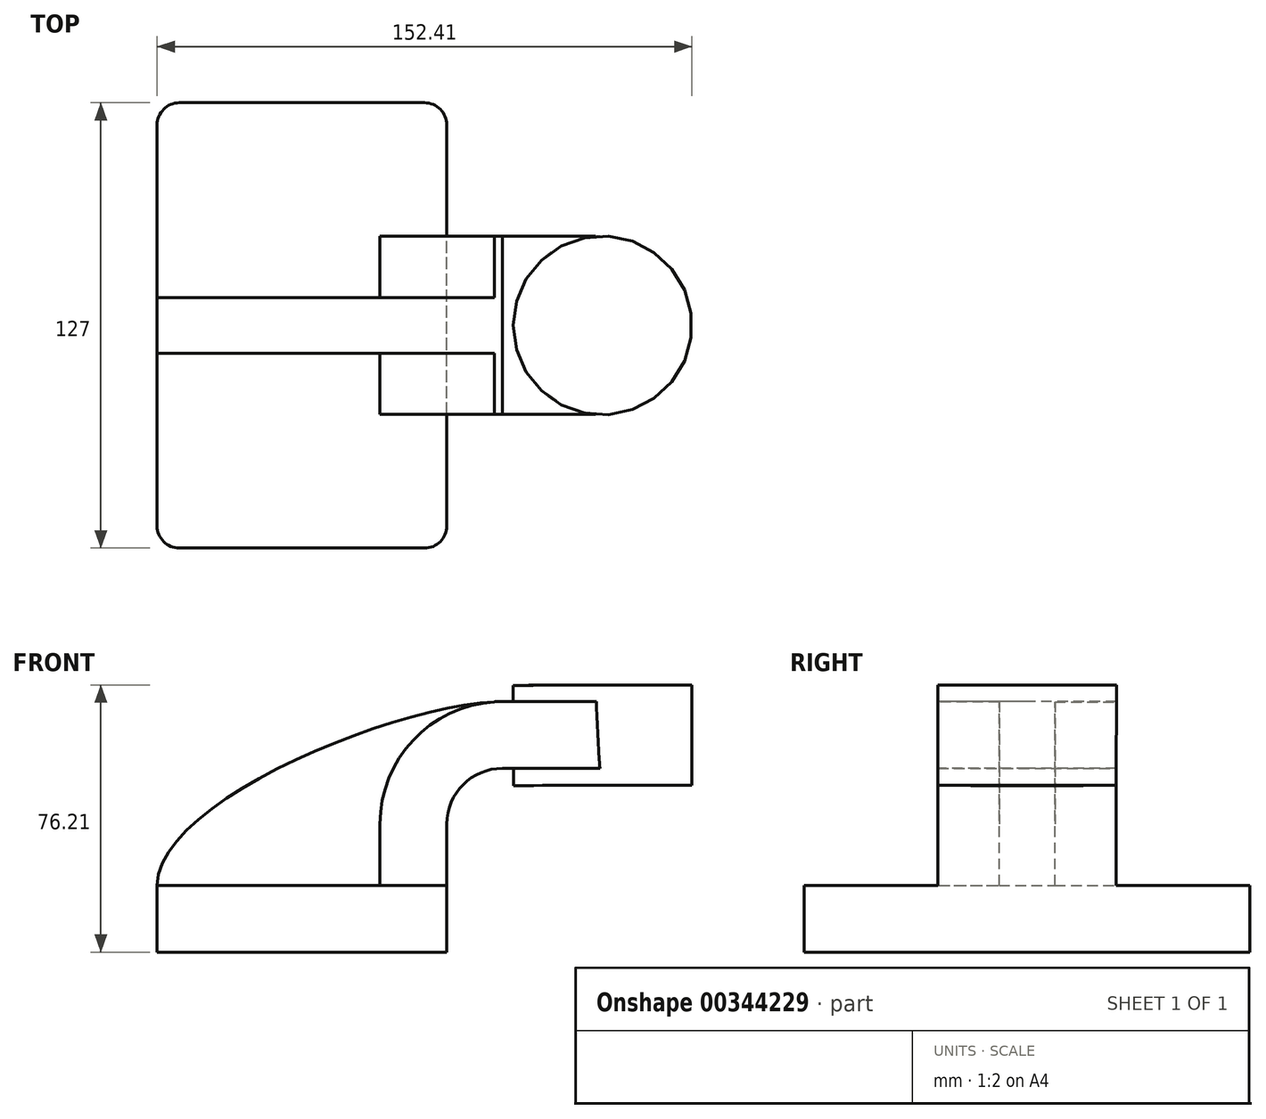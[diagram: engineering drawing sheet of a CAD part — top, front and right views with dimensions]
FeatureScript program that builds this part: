
annotation { "Feature Type Name" : "Feature", "Feature Type Description" : "" }
export const myFeature = defineFeature(function(context is Context, id is Id, definition is map)
    precondition{}
    {
        {
            var Q0;
            Q0=qCreatedBy(makeId("Front.planeOp"),FACE);
            var sketch = newSketch(context, id + "F0", { "sketchPlane" : qUnion([Q0])});
            skLineSegment(sketch, "E0.bottom", {"start": v(-41.27, -9.53) * mm, "end": v(41.28, -9.53) * mm});
            skLineSegment(sketch, "E0.top", {"start": v(-41.28, 9.52) * mm, "end": v(41.28, 9.52) * mm});
            skLineSegment(sketch, "E0.left", {"start": v(-41.28, -9.53) * mm, "end": v(-41.28, 9.52) * mm});
            skLineSegment(sketch, "E0.right", {"start": v(41.28, -9.53) * mm, "end": v(41.28, 9.52) * mm});
            skPoint(sketch, "E0.middle", {"position": v(0, 0) * mm});
            skLineSegment(sketch, "E1.bottom", {"start": v(60.32, 66.68) * mm, "end": v(111.12, 66.68) * mm});
            skLineSegment(sketch, "E1.top", {"start": v(60.33, 38.1) * mm, "end": v(111.12, 38.1) * mm});
            skLineSegment(sketch, "E1.left", {"start": v(60.32, 66.68) * mm, "end": v(60.33, 38.1) * mm});
            skLineSegment(sketch, "E1.right", {"start": v(111.12, 66.68) * mm, "end": v(111.12, 38.1) * mm});
            skPoint(sketch, "E1.middle", {"position": v(85.72, 52.39) * mm});
            skLineSegment(sketch, "E2", {"start": v(41.28, 9.52) * mm, "end": v(41.28, 27) * mm});
            skArc(sketch, "E3", {"start": v(57.15, 42.88) * mm, "mid": v(45.92, 38.23) * mm, "end": v(41.27, 27) * mm});
            skLineSegment(sketch, "E4", {"start": v(57.15, 42.88) * mm, "end": v(60.33, 42.88) * mm});
            skLineSegment(sketch, "E5.0", {"start": v(57.15, 61.93) * mm, "end": v(85.65, 61.93) * mm});
            skArc(sketch, "E5.1", {"start": v(57.15, 61.93) * mm, "mid": v(32.45, 51.7) * mm, "end": v(22.23, 27) * mm});
            skLineSegment(sketch, "E5.2", {"start": v(22.22, 9.52) * mm, "end": v(22.22, 27) * mm});
            skFitSpline(sketch, "E6", {"points": [v(-41.28, 9.53) * mm, v(57.15, 61.93) * mm], "startDerivative": vector(0.82, 73.3) * mm, "endDerivative": vector(87.78, 0.92) * mm});
            skLineSegment(sketch, "E7", {"start": v(60.33, 42.88) * mm, "end": v(85.65, 42.88) * mm});
            skLineSegment(sketch, "E8", {"start": v(85.65, 61.93) * mm, "end": v(85.65, 42.88) * mm});
            skLineSegment(sketch, "E9", {"start": v(85.72, 38.1) * mm, "end": v(85.65, 66.68) * mm});
            skSolve(sketch);
        }
        {
            var Q0;
            Q0=makeQuery(id+"F0.imprint","IMPRINT",FACE,{"disambiguationData":[TD([[makeQuery(id+"F0.imprint","IMPRINT",EDGE,{"derivedFrom":sQuery(id+"F0.wireOp",EDGE,"E0.bottom")}),1.0]])]});
            extrude(context, id + "F1", {"entities" : qUnion([Q0]), "endBound" : BoundingType.SYMMETRIC, "depth" : 127 * mm});
        }
        {
            var Q0;
            {var subQ3=sQuery(id+"F0.wireOp",EDGE,"E5.2");Q0=makeQuery(id+"F0.imprint","IMPRINT",FACE,{"disambiguationData":[TD([[makeQuery(id+"F0.imprint","IMPRINT",EDGE,{"derivedFrom":subQ3}),1.0]])]});}
            extrude(context, id + "F2", {"entities" : qUnion([Q0]), "operationType" : NewBodyOperationType.ADD, "endBound" : BoundingType.SYMMETRIC, "depth" : 15.88 * mm});
        }
        {
            var Q0;
            {var subQ0=sQuery(id+"F0.wireOp",EDGE,"E2");Q0=makeQuery(id+"F0.imprint","IMPRINT",FACE,{"disambiguationData":[TD([[makeQuery(id+"F0.imprint","IMPRINT",EDGE,{"derivedFrom":subQ0}),1.0]])]});}
            extrude(context, id + "F3", {"entities" : qUnion([Q0]), "operationType" : NewBodyOperationType.ADD, "endBound" : BoundingType.SYMMETRIC, "depth" : 50.8 * mm});
        }
        {
            var Q0;
            {var subQ0=sQuery(id+"F0.wireOp",EDGE,"E7");Q0=makeQuery(id+"F0.imprint","IMPRINT",FACE,{"disambiguationData":[TD([[makeQuery(id+"F0.imprint","IMPRINT",EDGE,{"derivedFrom":subQ0}),1.0]])]});}
            extrude(context, id + "F4", {"entities" : qUnion([Q0]), "operationType" : NewBodyOperationType.ADD, "endBound" : BoundingType.SYMMETRIC, "depth" : 50.8 * mm});
        }
        {
            var Q0;
            {var subQ0=sQuery(id+"F0.wireOp",EDGE,"E1.right");Q0=makeQuery(id+"F0.imprint","IMPRINT",FACE,{"disambiguationData":[TD([[makeQuery(id+"F0.imprint","IMPRINT",EDGE,{"derivedFrom":subQ0}),-1.0]])]});}
            var Q1;
            Q1=sQuery(id+"F0.wireOp",EDGE,"E9");
            revolve(context, id + "F5", {"operationType" : NewBodyOperationType.ADD, "entities" : qUnion([Q0]), "axis" : qUnion([Q1]), "revolveType" : RevolveType.FULL});
        }
        {
            var Q0;
            Q0=makeQuery(id+"F1.opExtrude","CAP_EDGE",EDGE,{"disambiguationData":[OSD([sQuery(id+"F0.wireOp",EDGE,"E0.right")])],"isStart":false});
            var Q1;
            Q1=makeQuery(id+"F1.opExtrude","CAP_EDGE",EDGE,{"disambiguationData":[OSD([sQuery(id+"F0.wireOp",EDGE,"E0.right")])],"isStart":true});
            var Q2;
            Q2=makeQuery(id+"F1.opExtrude","CAP_EDGE",EDGE,{"disambiguationData":[OSD([sQuery(id+"F0.wireOp",EDGE,"E0.left")])],"isStart":true});
            var Q3;
            Q3=makeQuery(id+"F1.opExtrude","CAP_EDGE",EDGE,{"disambiguationData":[OSD([sQuery(id+"F0.wireOp",EDGE,"E0.left")])],"isStart":false});
            fillet(context, id + "F6", {"entities" : qUnion([Q0, Q1, Q2, Q3]), "radius" : 6.35 * mm, "tangentPropagation" : true, "allowEdgeOverflow" : false});
        }
    });
